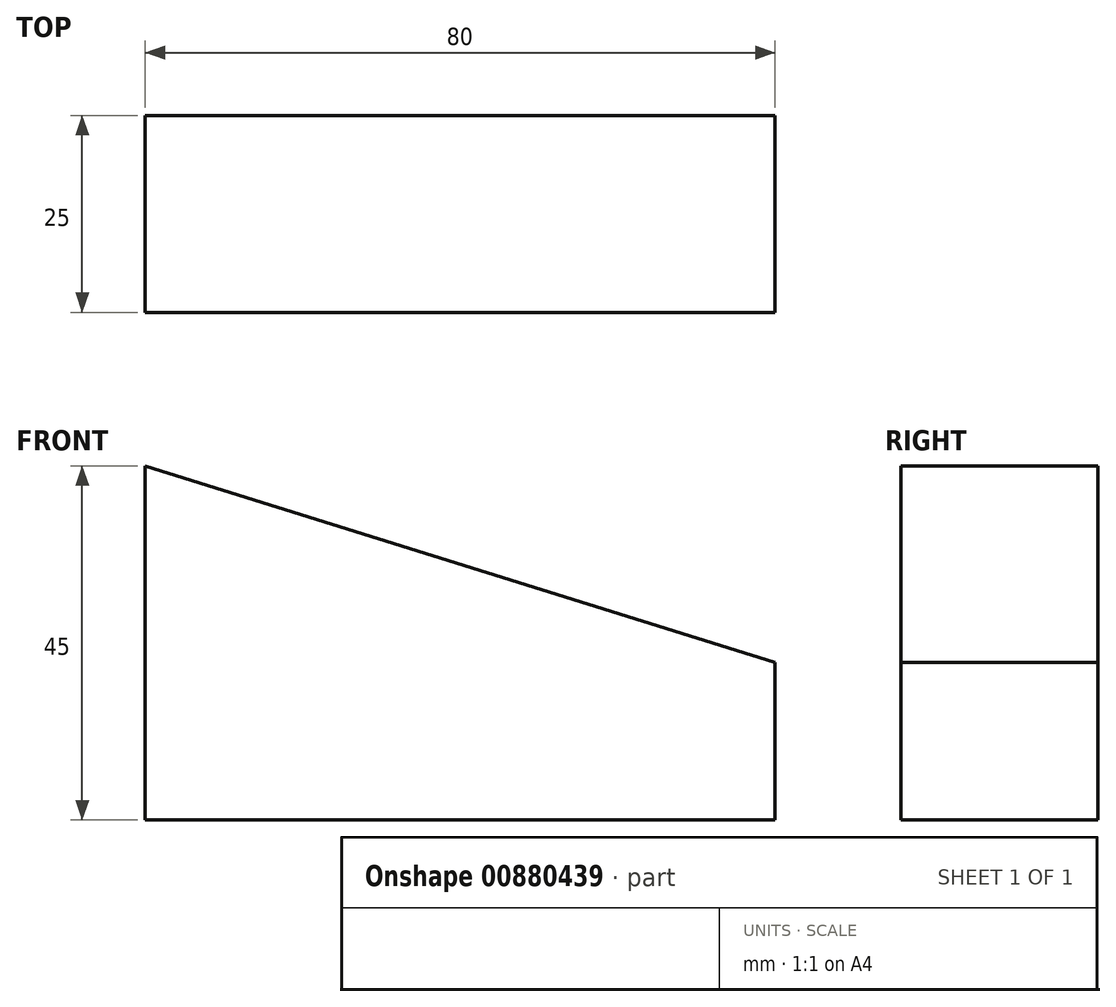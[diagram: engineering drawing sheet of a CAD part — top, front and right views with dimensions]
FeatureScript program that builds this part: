
annotation { "Feature Type Name" : "Feature", "Feature Type Description" : "" }
export const myFeature = defineFeature(function(context is Context, id is Id, definition is map)
    precondition{}
    {
        {
            var Q0;
            Q0=qCreatedBy(makeId("Front.planeOp"),FACE);
            var sketch = newSketch(context, id + "F0", { "sketchPlane" : qUnion([Q0])});
            skLineSegment(sketch, "E0", {"start": v(0, 0) * mm, "end": v(80, 0) * mm});
            skLineSegment(sketch, "E1", {"start": v(80, 0) * mm, "end": v(80, 20) * mm});
            skLineSegment(sketch, "E2", {"start": v(80, 20) * mm, "end": v(0, 45) * mm});
            skLineSegment(sketch, "E3", {"start": v(0, 45) * mm, "end": v(0, 0) * mm});
            skSolve(sketch);
        }
        {
            var Q0;
            Q0=makeQuery(id+"F0.imprint","IMPRINT",FACE,{"disambiguationData":[TD([[makeQuery(id+"F0.imprint","IMPRINT",EDGE,{"derivedFrom":sQuery(id+"F0.wireOp",EDGE,"E0")}),1.0]])]});
            extrude(context, id + "F1", {"entities" : qUnion([Q0]), "depth" : 25 * mm, "offsetDistance" : 25 * mm});
        }
    });
